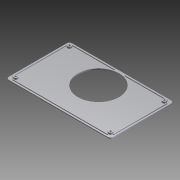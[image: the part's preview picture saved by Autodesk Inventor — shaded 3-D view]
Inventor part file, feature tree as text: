
AUTODESK INVENTOR PART (.ipt)
format: ipt  version: 2015 (Build 190159000, 159)  size: 182,784 bytes
history: native  units: in
note: dims shown in document units (in); Inventor stores cm internally (conversion verified against a paired STEP export)
features: other x3, extrude x1, imported_body x1
ambient origin geometry x8: Origin, YZ Plane, XZ Plane, XY Plane, X Axis, Y Axis, Z Axis, Center Point
bodies: Body1 (feature_tree)
feature tree (5):
  other  "Lid"
  other  "Cut-Extrude3"
  other  "Lid.ipt1"
  extrude  "Extrusion2"  Depth=1.506in
  imported_body  "Base1"
